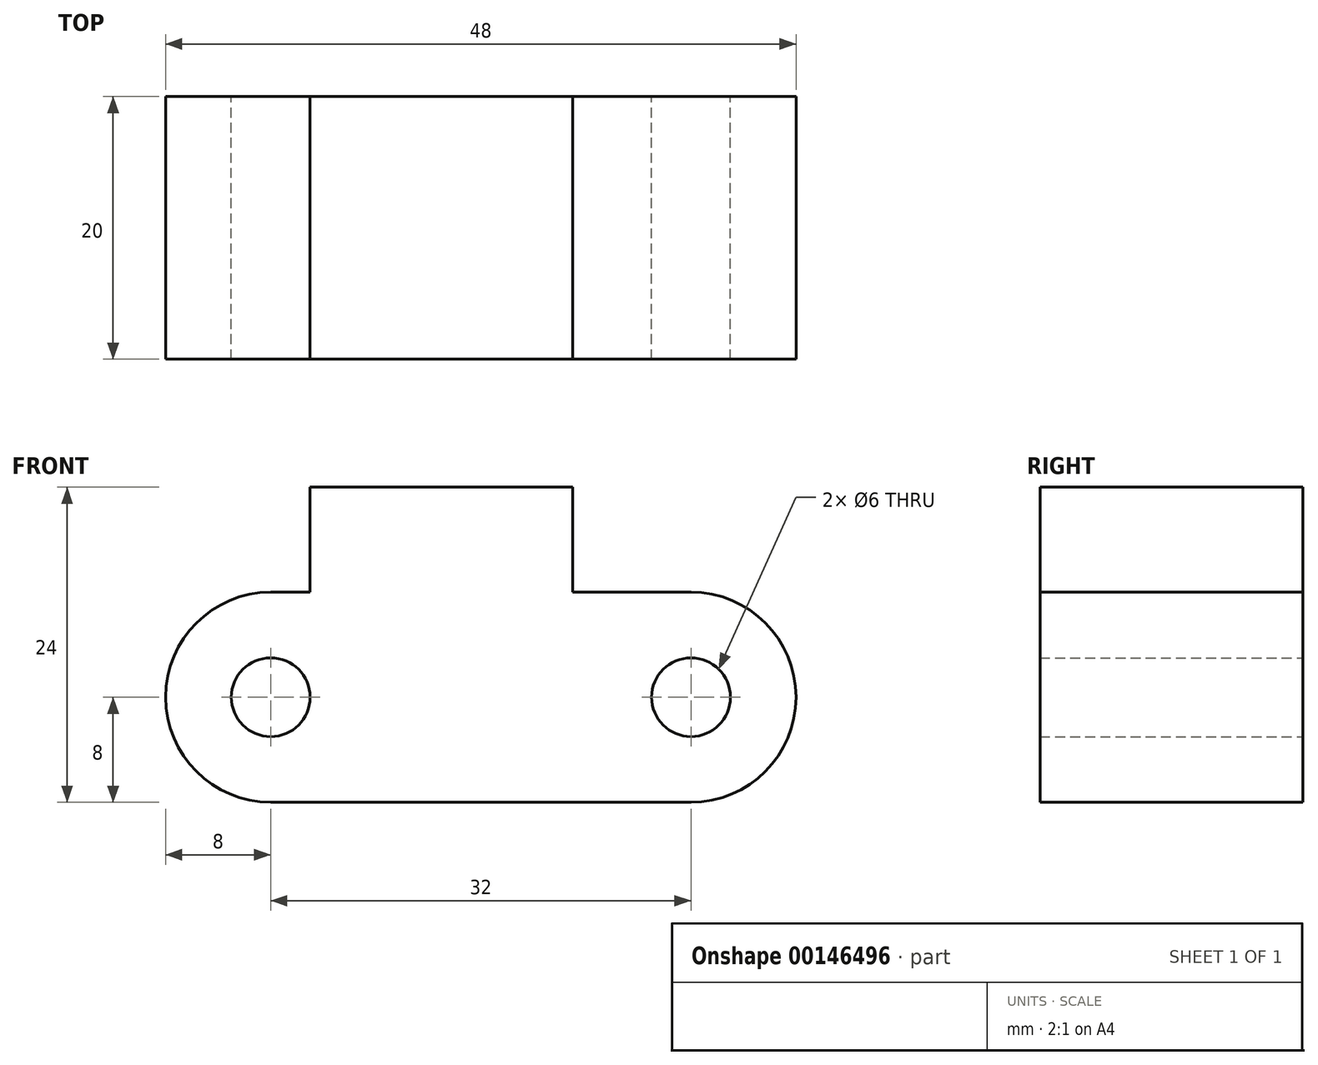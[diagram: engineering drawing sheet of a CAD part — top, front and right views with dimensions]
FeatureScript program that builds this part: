
annotation { "Feature Type Name" : "Feature", "Feature Type Description" : "" }
export const myFeature = defineFeature(function(context is Context, id is Id, definition is map)
    precondition{}
    {
        {
            var Q0;
            Q0=qCreatedBy(makeId("Front.planeOp"),FACE);
            var sketch = newSketch(context, id + "F0", { "sketchPlane" : qUnion([Q0])});
            skCircle(sketch, "E0", {"center": v(-16, 0) * mm, "radius": 3 * mm});
            skCircle(sketch, "E1.MirrorC", {"center": v(16, 0) * mm, "radius": 3 * mm});
            skArc(sketch, "E2", {"start": v(-16, 8) * mm, "mid": v(-24, 0) * mm, "end": v(-16, -8) * mm});
            skArc(sketch, "E3.MirrorCS", {"start": v(16, 8) * mm, "mid": v(24, 0) * mm, "end": v(16, -8) * mm});
            skLineSegment(sketch, "E4", {"start": v(-16, 8) * mm, "end": v(-13.02, 8) * mm});
            skLineSegment(sketch, "E5", {"start": v(-13.02, 8) * mm, "end": v(-13.02, 16) * mm});
            skLineSegment(sketch, "E6", {"start": v(-13.02, 16) * mm, "end": v(6.98, 16) * mm});
            skLineSegment(sketch, "E7", {"start": v(6.98, 16) * mm, "end": v(6.98, 8) * mm});
            skLineSegment(sketch, "E8", {"start": v(6.98, 8) * mm, "end": v(16, 8) * mm});
            skLineSegment(sketch, "E9", {"start": v(-16, -8) * mm, "end": v(16, -8) * mm});
            skSolve(sketch);
        }
        {
            var Q0;
            Q0=makeQuery(id+"F0.imprint","IMPRINT",FACE,{"disambiguationData":[TD([[makeQuery(id+"F0.imprint","IMPRINT",EDGE,{"derivedFrom":sQuery(id+"F0.wireOp",EDGE,"E0")}),-1.0]])]});
            extrude(context, id + "F1", {"entities" : qUnion([Q0]), "depth" : 20 * mm});
        }
    });
